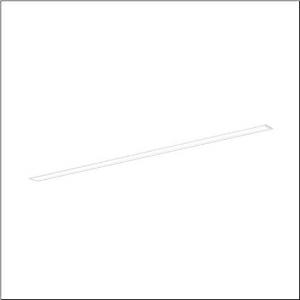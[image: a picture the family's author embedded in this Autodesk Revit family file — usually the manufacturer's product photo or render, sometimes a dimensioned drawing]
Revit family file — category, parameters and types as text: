
# Revit family: silica_r__21_51mx13db35wb_9931
name_source: partatom
category: Lighting Fixtures
units: mm (PartAtom-declared; Revit-internal decimal feet)

## family parameters
Cut with Voids When Loaded = No
Host = Face
Light Source = No
Part Type = Normal
Room Calculation Point = No
Round Connector Dimension = Use Diameter
Shared = No

## types (1)
- --- (1 x LED, 4100 lm, 30.1 W, 3000K)
    Apparent Load = 30 VA
    CIE Flux Codes = 78 96 99 100 100
    Color Rendering = 80
    Color Temperature = 3000K
    Default Elevation = 1800 mm
    Description = Silica® 21, office luminaire, primary optical cover: prismatic diffuser, of PMMA, CAT 2 (L<= 3000cd/m²), light emission: direct distribution, primary light characteristic: symmetric, installation type: recessed, LED, rated luminous flux: 4.100lm, luminous efficacy: 136lm/W, light colour: 830, colour temperature: 3000K, control gear: DALI 2, with terminal, 3+2-pole, max. 2.5mm², mains connection: 220..240V, AC, 50/60Hz, rated input power: 30.1W, luminaire housing, of aluminium, traffic white (RAL 9016), length: 1.528mm, width: 79mm, height: 53mm, protection rating (complete): IP20, insulation class (complete): insulation class I (protective earthing), certification: CE, ENEC, VDE, permissible operating ambient temperature: 0..+35°C, standard: EN 50419, packaging unit: 1 piece
    Height = 0 mm  [stored 0 ft]
    Lamp = 1 x LED
    Lamp Light Flux = 4100 lm
    Lamp Power = 30.1 W
    Lamp count = 1
    Length = 1527 mm
    Luminous efficacy = 136 lm/W
    Manufacturer = Siteco
    ModVariant = No
    Model = 51MX13DB35WB
    Mounting Place = Ceiling
    Mounting Type = Recessed
    Number of Poles = 1
    OnlyDefault = Yes
    Power Factor = 1
    Product Name = Silica® 21
    Product group = office luminaire | ceiling recessed
    ProductGroupID = 400
    Protection Class = Protection class I
    Protection Degree = IP 20
    RLX_Detail_Level = 1
    RLX_Emergency_Light_Flux = 0 lm
    RLX_Emergency_Type = 0
    RLX_Emergency_Type_DB = No
    RlxData = <blob elided: 14265 chars, md5=7acae619>
    Socket = socket
    Standby Power = 0 W
    System Light Flux = 4100 lm
    System Power = 30 W
    Type Comments = factory setting: luminous flux: 100 % | dim-lin: 254 | 345 mA
    Type Image = l_1251692.jpg
    URL = http://relux.com
    VarID = @adj_140565
    Voltage = 0 V
    Weight = 0.00 kg
    Width = 79 mm

note: [stored X ft] marks values corroborated as IEEE doubles in the binary element streams (Revit-internal decimal feet)

## geometry (parser evidence)
native form markers: Sweep x12
no freeform markers — native parametric forms only
